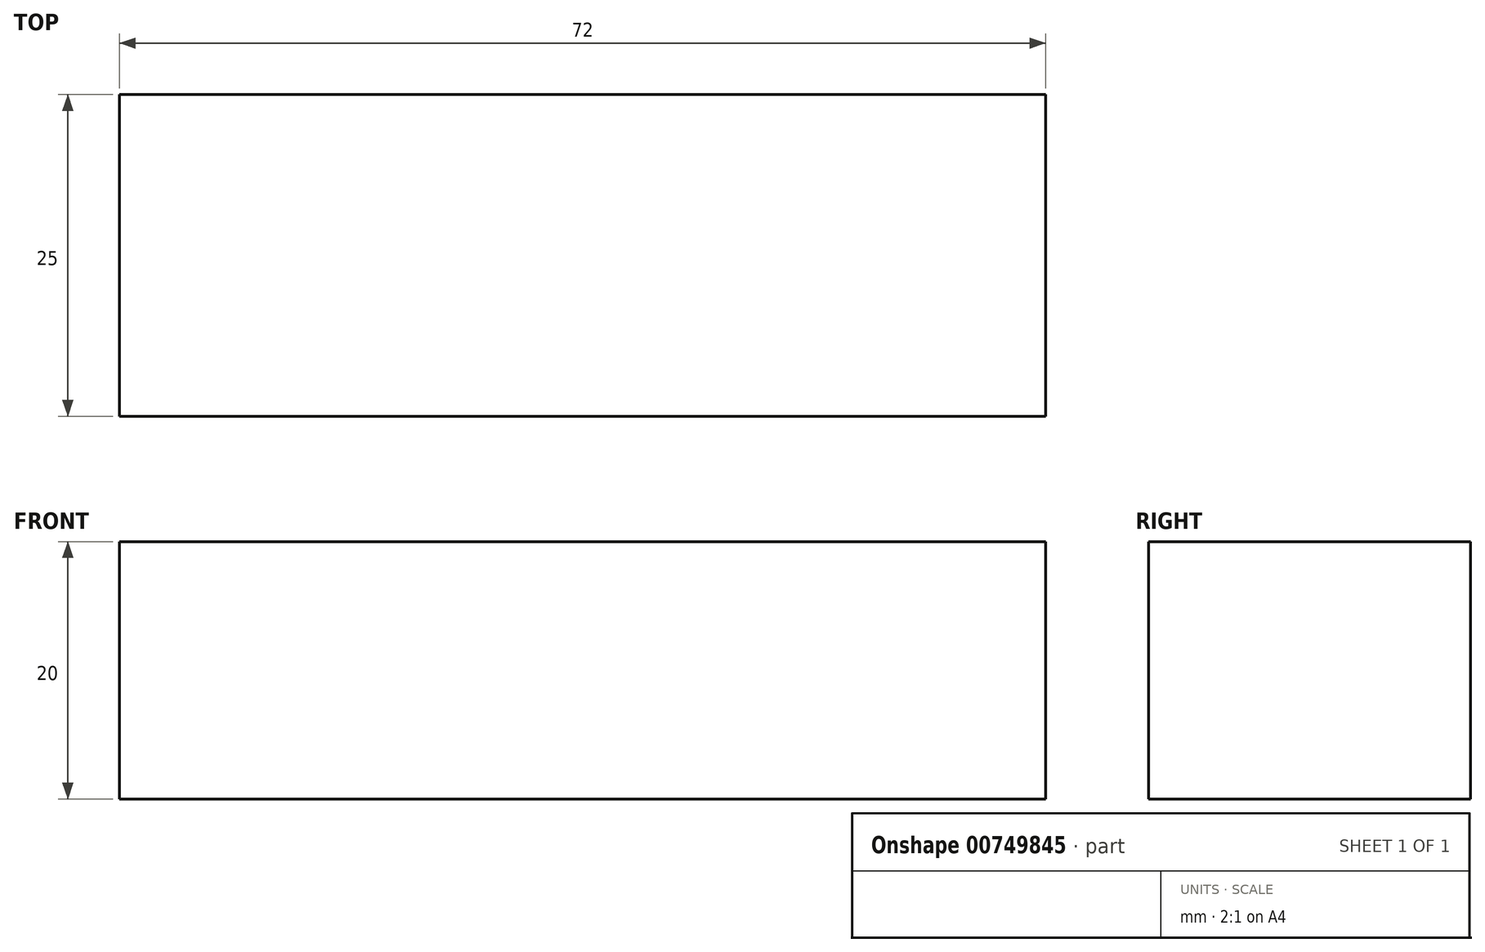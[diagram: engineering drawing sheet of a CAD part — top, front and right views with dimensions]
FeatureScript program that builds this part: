
annotation { "Feature Type Name" : "Feature", "Feature Type Description" : "" }
export const myFeature = defineFeature(function(context is Context, id is Id, definition is map)
    precondition{}
    {
        {
            var Q0;
            Q0=qCreatedBy(makeId("Front.planeOp"),FACE);
            var sketch = newSketch(context, id + "F0", { "sketchPlane" : qUnion([Q0])});
            skLineSegment(sketch, "E0.bottom", {"start": v(36, 10) * mm, "end": v(-36, 10) * mm});
            skLineSegment(sketch, "E0.top", {"start": v(36, -10) * mm, "end": v(-36, -10) * mm});
            skLineSegment(sketch, "E0.left", {"start": v(36, 10) * mm, "end": v(36, -10) * mm});
            skLineSegment(sketch, "E0.right", {"start": v(-36, 10) * mm, "end": v(-36, -10) * mm});
            skPoint(sketch, "E0.middle", {"position": v(0, 0) * mm});
            skSolve(sketch);
        }
        {
            var Q0;
            Q0 = qSketchRegion(id + "F0", true);
            extrude(context, id + "F1", {"entities" : qUnion([Q0]), "depth" : 25 * mm, "offsetDistance" : 25 * mm});
        }
    });
